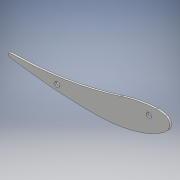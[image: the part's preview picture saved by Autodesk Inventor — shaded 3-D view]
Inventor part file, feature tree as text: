
AUTODESK INVENTOR PART (.ipt)
format: ipt  version: 2018.2 (Build 222227000, 227)  size: 123,392 bytes
history: native  units: mm
features: extrude x2, sketch x2, projected_geometry x1
ambient origin geometry x8: Origin, YZ Plane, XZ Plane, XY Plane, X Axis, Y Axis, Z Axis, Center Point
bodies: Body1 (feature_tree)
feature tree (5):
  extrude  "押し出し1"  Depth=4.0mm TaperAngle=0.0deg
  extrude  "押し出し2"  Depth=290.0mm
  sketch  "スケッチ1"
  projected_geometry  "投影ループ1"
  sketch  "スケッチ2"
